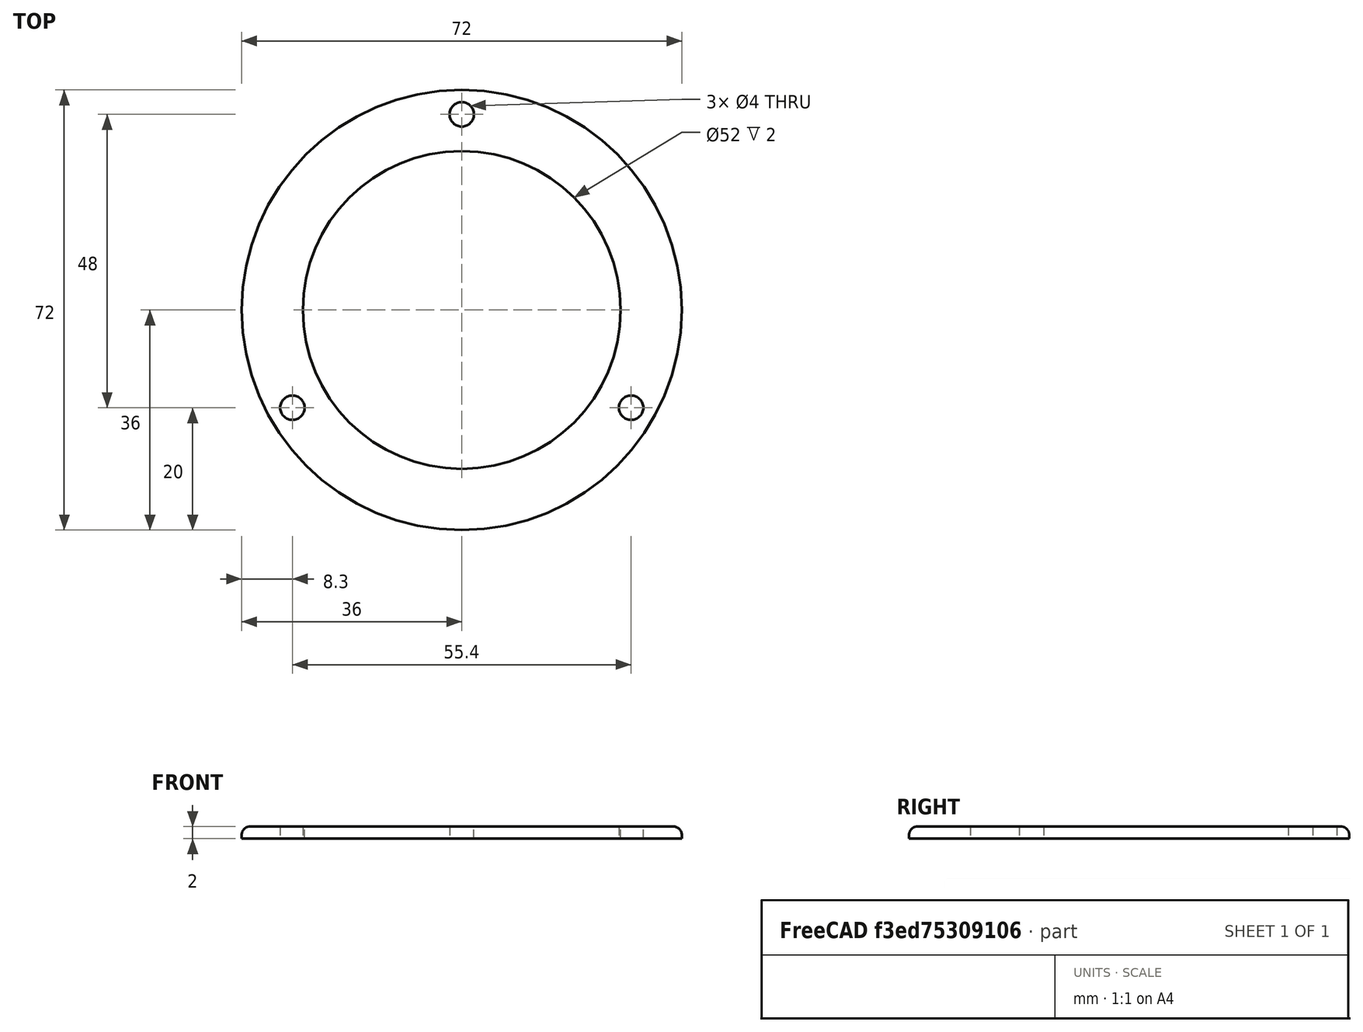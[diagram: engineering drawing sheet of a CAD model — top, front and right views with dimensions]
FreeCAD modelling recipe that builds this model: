
FCSTD DOCUMENT  (FreeCAD 0.20R29177 (Git))
Label: gauges
License: All rights reserved
LicenseURL: http://en.wikipedia.org/wiki/All_rights_reserved
objects: Part::Cylinder×5, Part::Cut×2, Part::MultiFuse×1, Part::Fillet×1
note: 9 computed .brp shape members not serialized (recipe doc carries the construction recipe); baked Part::Feature solids carry a one-line shape summary decoded from their .brp

FEATURE [Part::Cylinder] Cylinder
  Angle = 360
  AttacherType = Attacher::AttachEngine3D
  FirstAngle = 0
  Height = 2
  Radius = 36
  SecondAngle = 0
FEATURE [Part::Cylinder] Cylinder001
  Angle = 360
  AttacherType = Attacher::AttachEngine3D
  FirstAngle = 0
  Height = 10
  Radius = 26
  SecondAngle = 0
FEATURE [Part::Cylinder] Cylinder006
  Angle = 360
  AttacherType = Attacher::AttachEngine3D
  FirstAngle = 0
  Height = 10
  Placement = pos=(-27.7,-16,0) rot=(0,0,1;0rad)
  Radius = 2
  SecondAngle = 0
FEATURE [Part::Cylinder] Cylinder005
  Angle = 360
  AttacherType = Attacher::AttachEngine3D
  FirstAngle = 0
  Height = 10
  Placement = pos=(0,32,0) rot=(0,0,1;0rad)
  Radius = 2
  SecondAngle = 0
FEATURE [Part::Cylinder] Cylinder007
  Angle = 360
  AttacherType = Attacher::AttachEngine3D
  FirstAngle = 0
  Height = 10
  Placement = pos=(27.7,-16,0) rot=(0,0,1;0rad)
  Radius = 2
  SecondAngle = 0
FEATURE [Part::Cut] Cut
  Base = -> Cylinder
  Tool = -> Cylinder001
FEATURE [Part::MultiFuse] Fusion
  Shapes = -> [Cylinder007,Cylinder005,Cylinder006]
FEATURE [Part::Cut] Cut001
  Base = -> Cut
  Tool = -> Fusion
FEATURE [Part::Fillet] Fillet  label="2in-ring"
  Base = -> Cut001
  Edges = 1 edges r=1.4: [Edge3]
